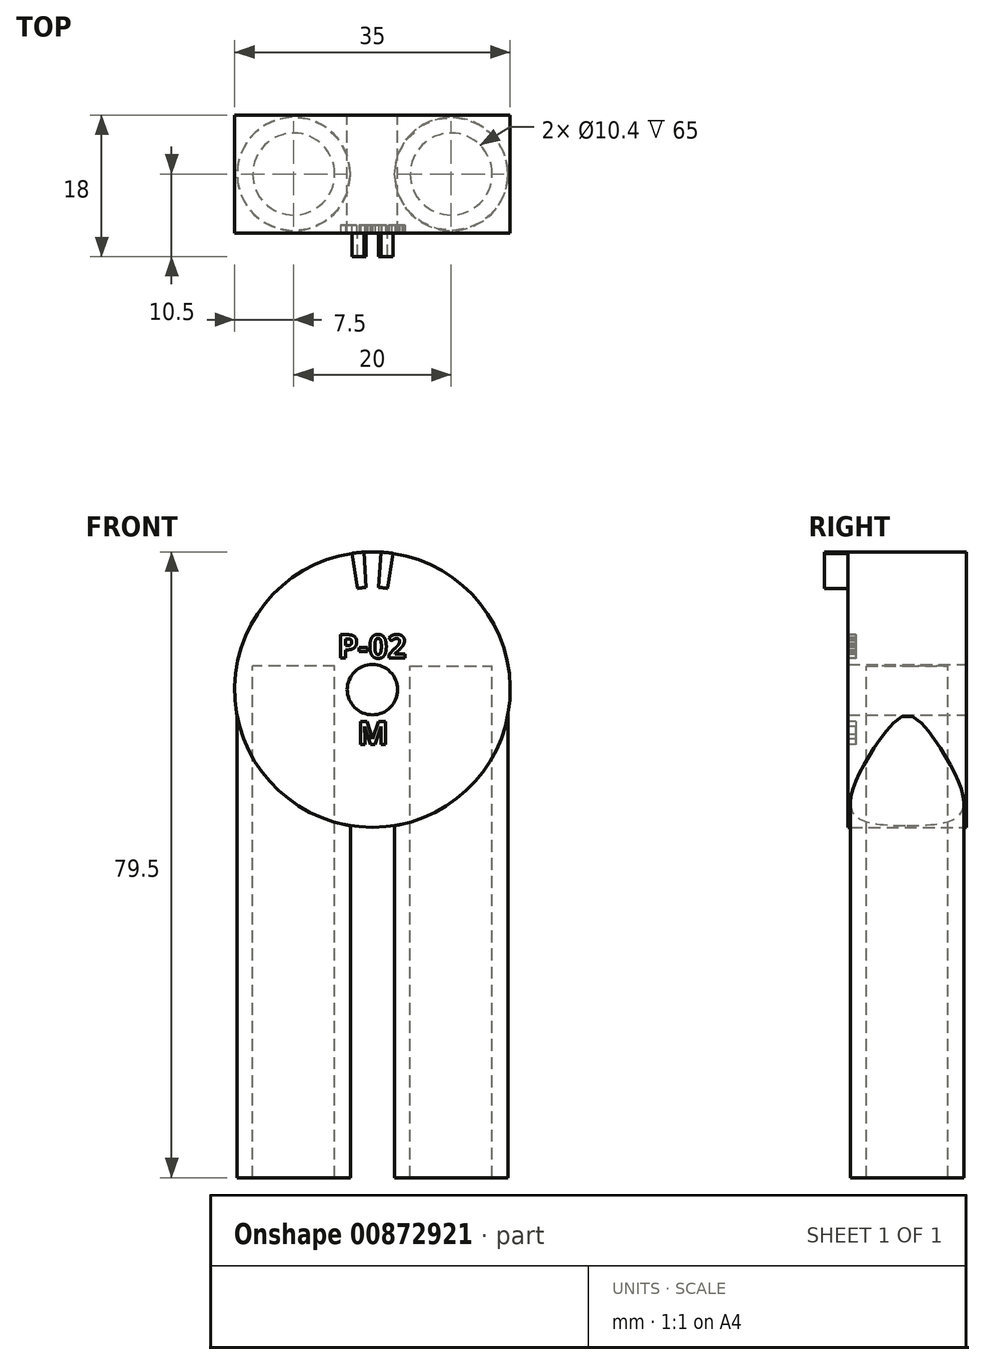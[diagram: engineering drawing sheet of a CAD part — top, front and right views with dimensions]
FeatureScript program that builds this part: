
annotation { "Feature Type Name" : "Feature", "Feature Type Description" : "" }
export const myFeature = defineFeature(function(context is Context, id is Id, definition is map)
    precondition{}
    {
        {
            var Q0;
            Q0=qCreatedBy(makeId("Front.planeOp"),FACE);
            var sketch = newSketch(context, id + "F0", { "sketchPlane" : qUnion([Q0])});
            skCircle(sketch, "E0", {"center": v(0, 0) * mm, "radius": 17.5 * mm});
            skCircle(sketch, "E1", {"center": v(0, 0) * mm, "radius": 3.2 * mm});
            skSolve(sketch);
        }
        {
            var Q0;
            Q0=qSketchRegion(id+"F0",true);
            extrude(context, id + "F1", {"entities" : qUnion([Q0]), "endBound" : BoundingType.SYMMETRIC, "depth" : 15 * mm, "offsetDistance" : 25 * mm});
        }
        {
            var Q0;
            Q0=makeQuery(id+"F1.opExtrude","CAP_FACE",FACE,{"disambiguationData":[OSD([sQuery(id+"F0.wireOp",EDGE,"E0")])],"isStart":false});
            var sketch = newSketch(context, id + "F2", { "sketchPlane" : qUnion([Q0])});
            skPoint(sketch, "E2.orphan", {"position": v(0, 0) * mm});
            skLineSegment(sketch, "E3", {"start": v(-42.27, 0) * mm, "end": v(49.07, 0) * mm, "construction": true});
            skLineSegment(sketch, "E4", {"start": v(0, -31.51) * mm, "end": v(0, 35.82) * mm, "construction": true});
            skArc(sketch, "E5", {"start": v(1.92, 12.86) * mm, "mid": v(1.36, 12.93) * mm, "end": v(0.8, 12.98) * mm});
            skArc(sketch, "E6", {"start": v(2.59, 17.3) * mm, "mid": v(1.83, 17.4) * mm, "end": v(1.07, 17.47) * mm});
            skLineSegment(sketch, "E7", {"start": v(0.8, 12.98) * mm, "end": v(1.07, 17.47) * mm});
            skLineSegment(sketch, "E8", {"start": v(2.59, 17.3) * mm, "end": v(1.92, 12.86) * mm});
            skLineSegment(sketch, "E9", {"start": v(0, 0) * mm, "end": v(1.83, 17.4) * mm, "construction": true});
            skSolve(sketch);
        }
        {
            var Q0;
            Q0=qSketchRegion(id+"F2",true);
            extrude(context, id + "F3", {"entities" : qUnion([Q0]), "operationType" : NewBodyOperationType.ADD, "depth" : 3 * mm, "offsetDistance" : 25 * mm});
        }
        {
            var Q0;
            Q0=qCreatedBy(makeId("Top.planeOp"),FACE);
            var sketch = newSketch(context, id + "F4", { "sketchPlane" : qUnion([Q0])});
            skCircle(sketch, "E10", {"center": v(-10, 0) * mm, "radius": 5.2 * mm});
            skSolve(sketch);
        }
        {
            var Q0;
            Q0=qSketchRegion(id+"F4",true);
            extrude(context, id + "F5", {"entities" : qUnion([Q0]), "operationType" : NewBodyOperationType.REMOVE, "oppositeDirection" : true, "depth" : 25 * mm, "offsetDistance" : 25 * mm, "hasSecondDirection" : true, "secondDirectionOppositeDirection" : false, "secondDirectionDepth" : 3 * mm});
        }
        {
            var Q0;
            Q0=qCreatedBy(makeId("Top.planeOp"),FACE);
            cPlane(context, id + "F6", {"entities" : qUnion([Q0]), "cplaneType" : CPlaneType.OFFSET, "offset" : 2 * mm, "oppositeDirection" : true, "width" : 150 * mm, "height" : 150 * mm});
        }
        {
            var Q0;
            Q0=qCreatedBy(id+"F6.planeOp",FACE);
            var sketch = newSketch(context, id + "F7", { "sketchPlane" : qUnion([Q0])});
            skCircle(sketch, "E11", {"center": v(-10, 0) * mm, "radius": 5.2 * mm});
            skCircle(sketch, "E12", {"center": v(-10, 0) * mm, "radius": 7.2 * mm});
            skSolve(sketch);
        }
        {
            var Q0;
            Q0=qSketchRegion(id+"F7",true);
            extrude(context, id + "F8", {"entities" : qUnion([Q0]), "operationType" : NewBodyOperationType.ADD, "oppositeDirection" : true, "depth" : 60 * mm, "offsetDistance" : 25 * mm});
        }
        {
            var Q0;
            Q0=makeQuery(id+"F1.opExtrude","SWEPT_BODY",BODY,{"disambiguationData":[OSD([sQuery(id+"F0.wireOp",EDGE,"E0"),sQuery(id+"F0.wireOp",EDGE,"E1")])]});
            var Q1;
            Q1=qCreatedBy(makeId("Right.planeOp"),FACE);
            mirror(context, id + "F9", {"entities" : qUnion([Q0]), "mirrorPlane" : qUnion([Q1])});
        }
        {
            var Q0;
            Q0=makeQuery(id+"F1.opExtrude","CAP_FACE",FACE,{"disambiguationData":[OSD([sQuery(id+"F0.wireOp",EDGE,"E0"),sQuery(id+"F0.wireOp",EDGE,"E1")])],"isStart":false});
            var sketch = newSketch(context, id + "F10", { "sketchPlane" : qUnion([Q0])});
            skText(sketch, "E13", { "text": "P-02", "fontName": "OpenSans-Bold.ttf"});
            const initialGuessF10  = {"E13": [-0.00443, 0.004, 1, 0, 0.003]};
            skSetInitialGuess(sketch, initialGuessF10);
            skSolve(sketch);
        }
        {
            var Q0;
            Q0=qSketchRegion(id+"F10",true);
            extrude(context, id + "F11", {"entities" : qUnion([Q0]), "operationType" : NewBodyOperationType.REMOVE, "oppositeDirection" : true, "depth" : 1 * mm, "offsetDistance" : 25 * mm});
        }
        {
            var Q0;
            {var subQ3=sQuery(id+"F0.wireOp",EDGE,"E1");var subQ5=sQuery(id+"F0.wireOp",EDGE,"E0");Q0=makeQuery(id+"F11.boolean.opBoolean","SPLIT",FACE,{"disambiguationData":[TD([makeQuery(id+"F9.opPattern","COPY",FACE,{"derivedFrom":makeQuery(id+"F1.opExtrude","SWEPT_FACE",FACE,{"disambiguationData":[OSD([subQ3])]}),"instanceName":"1"})])],"derivedFrom":makeQuery(id+"F9.opPattern","COPY",FACE,{"derivedFrom":makeQuery(id+"F1.opExtrude","CAP_FACE",FACE,{"disambiguationData":[OSD([subQ5,subQ3])],"isStart":false}),"instanceName":"1"})});}
            var sketch = newSketch(context, id + "F12", { "sketchPlane" : qUnion([Q0])});
            skText(sketch, "E14", { "text": "M", "fontName": "OpenSans-Bold.ttf"});
            const initialGuessF12  = {"E14": [-0.00191, -0.007, 1, 0, 0.003]};
            skSetInitialGuess(sketch, initialGuessF12);
            skSolve(sketch);
        }
        {
            var Q0;
            Q0=qSketchRegion(id+"F12",true);
            extrude(context, id + "F13", {"entities" : qUnion([Q0]), "operationType" : NewBodyOperationType.REMOVE, "oppositeDirection" : true, "depth" : 1 * mm, "offsetDistance" : 25 * mm});
        }
    });
